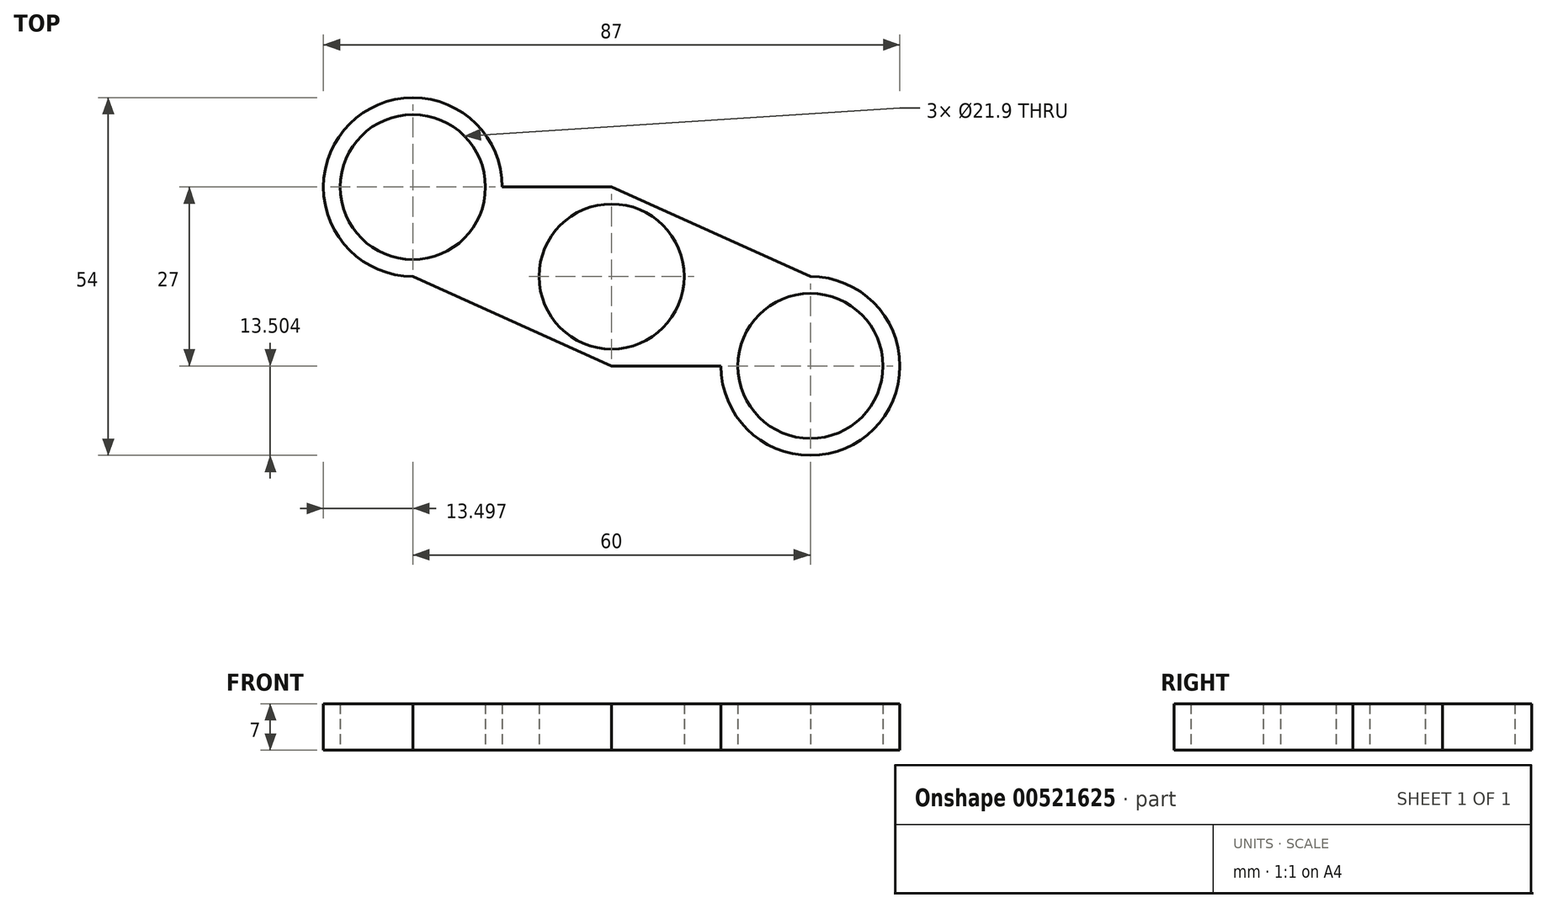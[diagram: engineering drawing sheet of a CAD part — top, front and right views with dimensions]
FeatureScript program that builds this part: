
annotation { "Feature Type Name" : "Feature", "Feature Type Description" : "" }
export const myFeature = defineFeature(function(context is Context, id is Id, definition is map)
    precondition{}
    {
        {
            var Q0;
            Q0=qCreatedBy(makeId("Top.planeOp"),FACE);
            var sketch = newSketch(context, id + "F0", { "sketchPlane" : qUnion([Q0])});
            skCircle(sketch, "E0", {"center": v(-14.08, 11.56) * mm, "radius": 13.5 * mm});
            skLineSegment(sketch, "E1", {"start": v(-14.08, -1.94) * mm, "end": v(15.92, -1.94) * mm});
            skLineSegment(sketch, "E2", {"start": v(-14.08, 25.06) * mm, "end": v(-44.08, 25.06) * mm});
            skCircle(sketch, "E3", {"center": v(-44.08, 25.06) * mm, "radius": 13.5 * mm});
            skCircle(sketch, "E4", {"center": v(15.92, -1.94) * mm, "radius": 13.5 * mm});
            skCircle(sketch, "E5", {"center": v(-44.08, 25.06) * mm, "radius": 10.95 * mm});
            skCircle(sketch, "E6", {"center": v(-14.08, 11.56) * mm, "radius": 10.95 * mm});
            skCircle(sketch, "E7", {"center": v(15.92, -1.94) * mm, "radius": 10.95 * mm});
            skLineSegment(sketch, "E8", {"start": v(-14.08, -1.94) * mm, "end": v(-44.08, 11.56) * mm});
            skLineSegment(sketch, "E9", {"start": v(-14.08, 25.06) * mm, "end": v(15.92, 11.56) * mm});
            skSolve(sketch);
        }
        {
            var Q0;
            Q0=makeQuery(id+"F0.imprint","IMPRINT",FACE,{"disambiguationData":[TD([[makeQuery(id+"F0.imprint","IMPRINT",EDGE,{"derivedFrom":sQuery(id+"F0.wireOp",EDGE,"E5")}),-1.0]])]});
            var Q1;
            {var subQ3=sQuery(id+"F0.wireOp",EDGE,"E8");var subQ5=sQuery(id+"F0.wireOp",EDGE,"E3");var subQ7=makeQuery(id+"F0.imprint","INTERSECT",VERTEX,{"derivedFrom":[subQ5,subQ3]});Q1=makeQuery(id+"F0.imprint","IMPRINT",FACE,{"disambiguationData":[TD([[makeQuery(id+"F0.imprint","IMPRINT",EDGE,{"disambiguationData":[TD([[subQ7,-1.0]])],"derivedFrom":subQ5}),-1.0]])]});}
            var Q2;
            Q2=makeQuery(id+"F0.imprint","IMPRINT",FACE,{"disambiguationData":[TD([[makeQuery(id+"F0.imprint","IMPRINT",EDGE,{"derivedFrom":sQuery(id+"F0.wireOp",EDGE,"E6")}),-1.0]])]});
            var Q3;
            {var subQ3=sQuery(id+"F0.wireOp",EDGE,"E9");var subQ5=sQuery(id+"F0.wireOp",EDGE,"E4");var subQ6=makeQuery(id+"F0.imprint","INTERSECT",VERTEX,{"derivedFrom":[subQ5,subQ3]});Q3=makeQuery(id+"F0.imprint","IMPRINT",FACE,{"disambiguationData":[TD([[makeQuery(id+"F0.imprint","IMPRINT",EDGE,{"disambiguationData":[TD([[subQ6,-1.0]])],"derivedFrom":subQ5}),-1.0]])]});}
            var Q4;
            Q4=makeQuery(id+"F0.imprint","IMPRINT",FACE,{"disambiguationData":[TD([[makeQuery(id+"F0.imprint","IMPRINT",EDGE,{"derivedFrom":sQuery(id+"F0.wireOp",EDGE,"E7")}),-1.0]])]});
            extrude(context, id + "F1", {"entities" : qUnion([Q0, Q1, Q2, Q3, Q4]), "depth" : 7 * mm, "offsetDistance" : 25 * mm});
        }
    });
